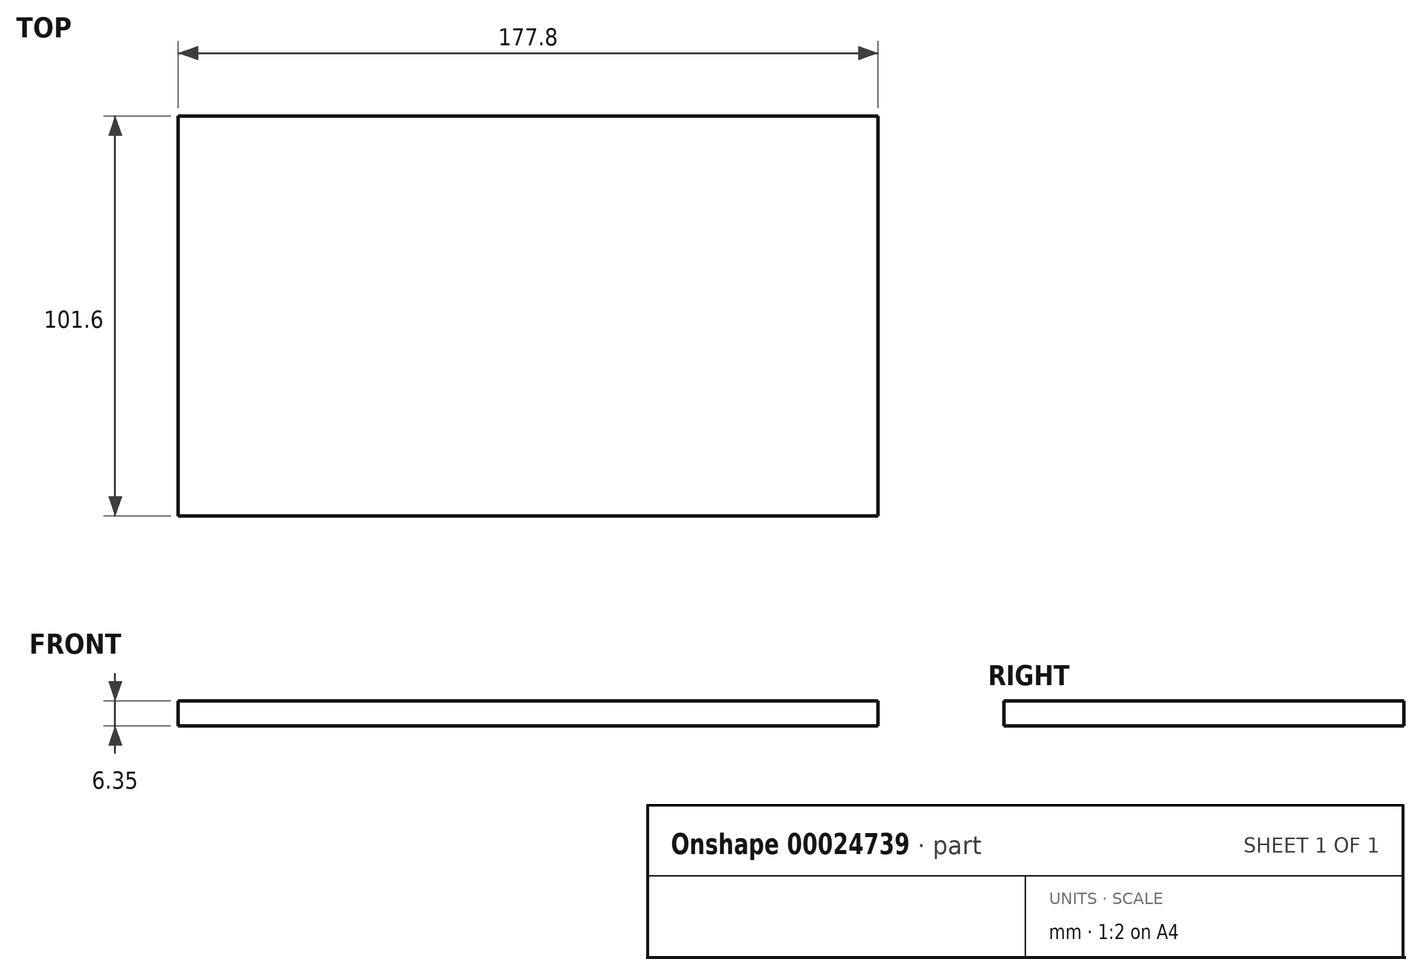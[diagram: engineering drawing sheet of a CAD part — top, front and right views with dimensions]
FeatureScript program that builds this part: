
annotation { "Feature Type Name" : "Feature", "Feature Type Description" : "" }
export const myFeature = defineFeature(function(context is Context, id is Id, definition is map)
    precondition{}
    {
        {
            var Q0;
            Q0=qCreatedBy(makeId("Top.planeOp"),FACE);
            var sketch = newSketch(context, id + "F0", { "sketchPlane" : qUnion([Q0])});
            skLineSegment(sketch, "E0.bottom", {"start": v(-93.33, 47.13) * mm, "end": v(84.47, 47.13) * mm});
            skLineSegment(sketch, "E0.top", {"start": v(-93.33, -54.47) * mm, "end": v(84.47, -54.47) * mm});
            skLineSegment(sketch, "E0.left", {"start": v(-93.33, 47.13) * mm, "end": v(-93.33, -54.47) * mm});
            skLineSegment(sketch, "E0.right", {"start": v(84.47, 47.13) * mm, "end": v(84.47, -54.47) * mm});
            skSolve(sketch);
        }
        {
            var Q0;
            Q0 = qSketchRegion(id + "F0", true);
            extrude(context, id + "F1", {"entities" : qUnion([Q0]), "depth" : 6.35 * mm});
        }
    });
